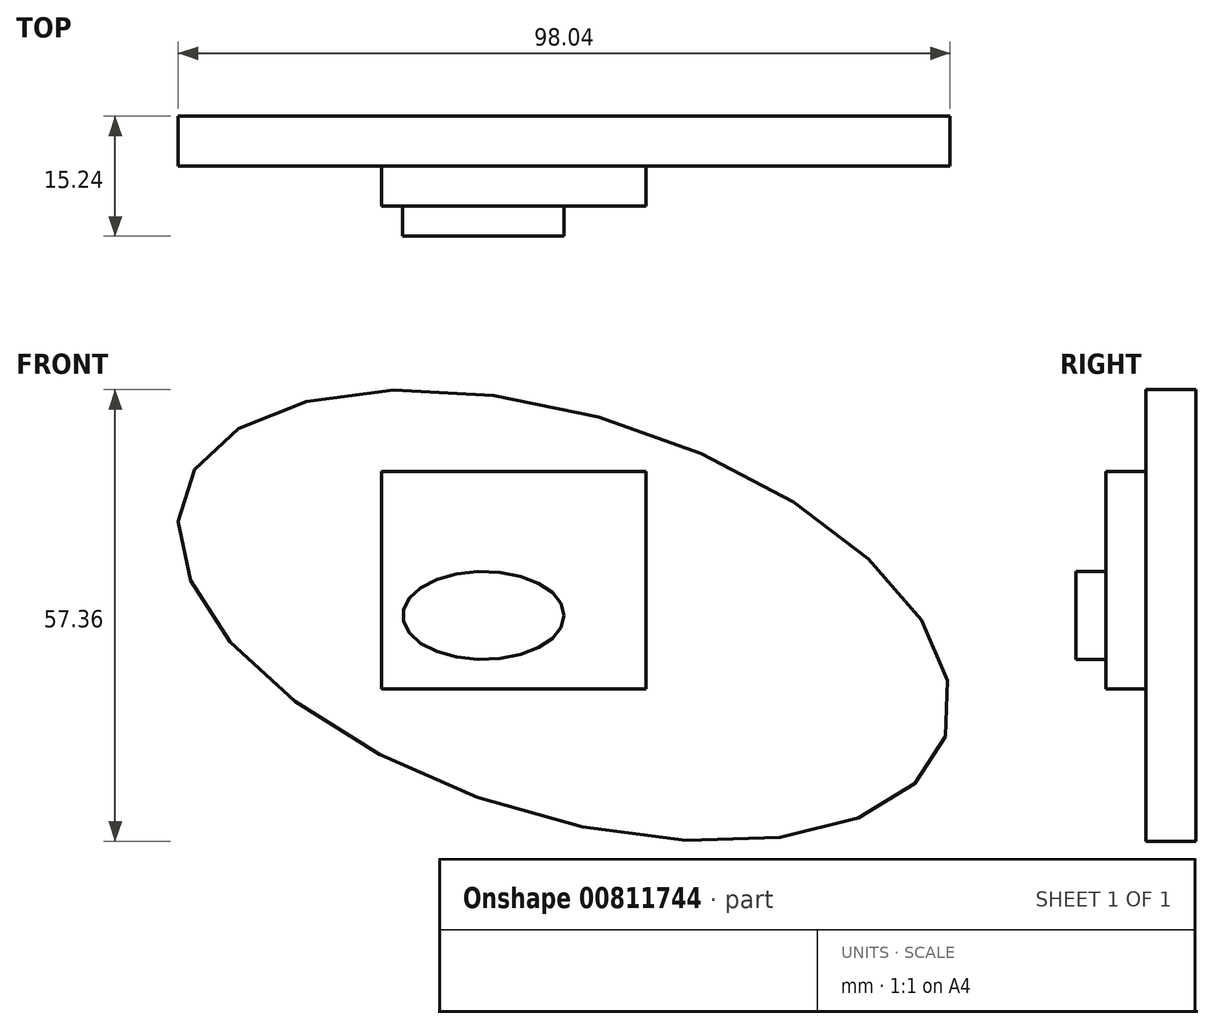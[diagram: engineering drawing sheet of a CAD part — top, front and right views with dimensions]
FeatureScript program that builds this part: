
annotation { "Feature Type Name" : "Feature", "Feature Type Description" : "" }
export const myFeature = defineFeature(function(context is Context, id is Id, definition is map)
    precondition{}
    {
        {
            var Q0;
            Q0=qCreatedBy(makeId("Front.planeOp"),FACE);
            var sketch = newSketch(context, id + "F0", { "sketchPlane" : qUnion([Q0])});
            skEllipse(sketch, "E0", {"center": v(0, 0) * mm, "majorRadius": 50.8 * mm, "minorRadius": 25.4 * mm, "majorAxis": v(0.95, -0.3)});
            skSolve(sketch);
        }
        {
            var Q0;
            Q0 = qSketchRegion(id + "F0", true);
            extrude(context, id + "F1", {"entities" : qUnion([Q0]), "depth" : 6.35 * mm, "offsetDistance" : 25.4 * mm});
        }
        {
            var Q0;
            Q0=makeQuery(id+"F1.opExtrude","CAP_FACE",FACE,{"disambiguationData":[OSD([sQuery(id+"F0.wireOp",EDGE,"E0")])],"isStart":false});
            var sketch = newSketch(context, id + "F2", { "sketchPlane" : qUnion([Q0])});
            skLineSegment(sketch, "E1.bottom", {"start": v(-23.2, 18.31) * mm, "end": v(10.4, 18.31) * mm});
            skLineSegment(sketch, "E1.top", {"start": v(-23.2, -9.34) * mm, "end": v(10.4, -9.34) * mm});
            skLineSegment(sketch, "E1.left", {"start": v(-23.2, 18.31) * mm, "end": v(-23.2, -9.34) * mm});
            skLineSegment(sketch, "E1.right", {"start": v(10.4, 18.31) * mm, "end": v(10.4, -9.34) * mm});
            skLineSegment(sketch, "E2.bottom", {"start": v(10.4, -9.34) * mm, "end": v(30.85, -9.34) * mm});
            skLineSegment(sketch, "E2.top", {"start": v(10.4, -19.14) * mm, "end": v(30.85, -19.14) * mm});
            skLineSegment(sketch, "E2.left", {"start": v(10.4, -9.34) * mm, "end": v(10.4, -19.14) * mm});
            skLineSegment(sketch, "E2.right", {"start": v(30.85, -9.34) * mm, "end": v(30.85, -19.14) * mm});
            skSolve(sketch);
        }
        {
            var Q0;
            Q0=makeQuery(id+"F2.imprint","IMPRINT",FACE,{"disambiguationData":[TD([[makeQuery(id+"F2.imprint","IMPRINT",EDGE,{"derivedFrom":sQuery(id+"F2.wireOp",EDGE,"E1.bottom")}),-1.0]])]});
            extrude(context, id + "F3", {"entities" : qUnion([Q0]), "operationType" : NewBodyOperationType.ADD, "depth" : 5.08 * mm, "offsetDistance" : 25.4 * mm});
        }
        {
            var Q0;
            Q0=makeQuery(id+"F3.opExtrude","CAP_FACE",FACE,{"disambiguationData":[OSD([sQuery(id+"F2.wireOp",EDGE,"E1.bottom"),sQuery(id+"F2.wireOp",EDGE,"E1.top"),sQuery(id+"F2.wireOp",EDGE,"E1.left"),sQuery(id+"F2.wireOp",EDGE,"E1.right")])],"isStart":false});
            var sketch = newSketch(context, id + "F4", { "sketchPlane" : qUnion([Q0])});
            skEllipse(sketch, "E3", {"center": v(-10.26, 0) * mm, "majorRadius": 10.26 * mm, "minorRadius": 5.58 * mm, "majorAxis": v(1, 0)});
            skSolve(sketch);
        }
        {
            var Q0;
            Q0=makeQuery(id+"F4.imprint","IMPRINT",FACE,{"disambiguationData":[TD([[makeQuery(id+"F4.imprint","IMPRINT",EDGE,{"derivedFrom":sQuery(id+"F4.wireOp",EDGE,"E3")}),1.0]])]});
            var Q1;
            Q1=sQuery(id+"F4.wireOp",EDGE,"E3");
            extrude(context, id + "F5", {"entities" : qUnion([Q0]), "operationType" : NewBodyOperationType.ADD, "surfaceOperationType" : NewSurfaceOperationType.ADD, "surfaceEntities" : qUnion([Q1]), "depth" : 3.8 * mm, "offsetDistance" : 25.4 * mm});
        }
    });
